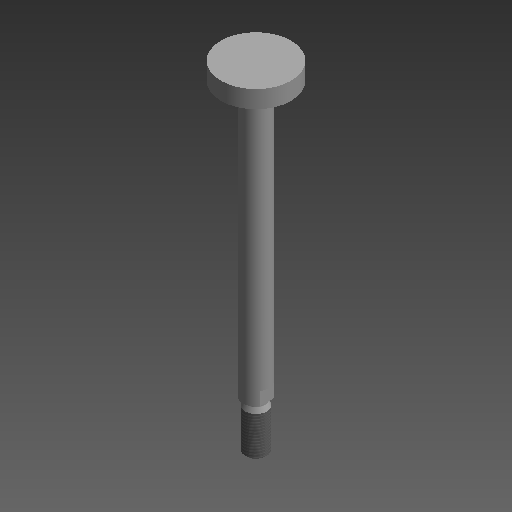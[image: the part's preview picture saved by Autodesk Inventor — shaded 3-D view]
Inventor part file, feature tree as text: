
AUTODESK INVENTOR PART (.ipt)
format: ipt  version: 2021 (Build 250183000, 183)  size: 149,504 bytes
history: native  units: mm (DEFAULTED — no unit token found)
features: other x28, sketch x3, revolve x2, thread x1, extrude x1
ambient origin geometry x8: Origin, YZ Plane, XZ Plane, XY Plane, X Axis, Y Axis, Z Axis, Center Point
bodies: Solid1 (feature_tree)
feature tree (35):
  revolve  "Revolution1"  Angle=360.0deg
  revolve  "Revolution2"  [1 undecoded]
  thread  "Thread1"  [1 undecoded]
  extrude  "Extrusion1"  [1 undecoded]
  other  "FDT_KSAUFSATZ_XY"
  other  "FDT_KSAUFSATZ_YZ"
  other  "FDT_KSAUFSATZ_ZX"
  other  "FDT_KSAUFSATZ_X"
  other  "FDT_KSAUFSATZ_Y"
  other  "FDT_KSAUFSATZ_Z"
  other  "FDT_KSAUFSATZ_Center"
  other  "FDT_NUT_XY"
  other  "FDT_NUT_YZ"
  other  "FDT_NUT_ZX"
  other  "FDT_NUT_X"
  other  "FDT_NUT_Y"
  other  "FDT_NUT_Z"
  other  "FDT_NUT_Center"
  other  "KS_XY"
  other  "KS_YZ"
  other  "KS_ZX"
  other  "KS_X"
  other  "KS_Y"
  other  "KS_Z"
  other  "KS_Center"
  other  "NUT1_XY"
  other  "NUT1_YZ"
  other  "NUT1_ZX"
  other  "NUT1_X"
  other  "NUT1_Y"
  other  "NUT1_Z"
  other  "NUT1_Center"
  sketch  "Sketch_2"  dims[d0=360.0deg d1=360.0deg]
  sketch  "Sketch_6"  dims[d2=17.535mm d3=0.0mm d4=7.0mm d5=0.0mm]
  sketch  "Sketch_7"
note: 3 required parameter values undecoded (feature->parameter linkage not recoverable at this tier; creation-order binding heuristic only, values carry confidence <= 0.55)